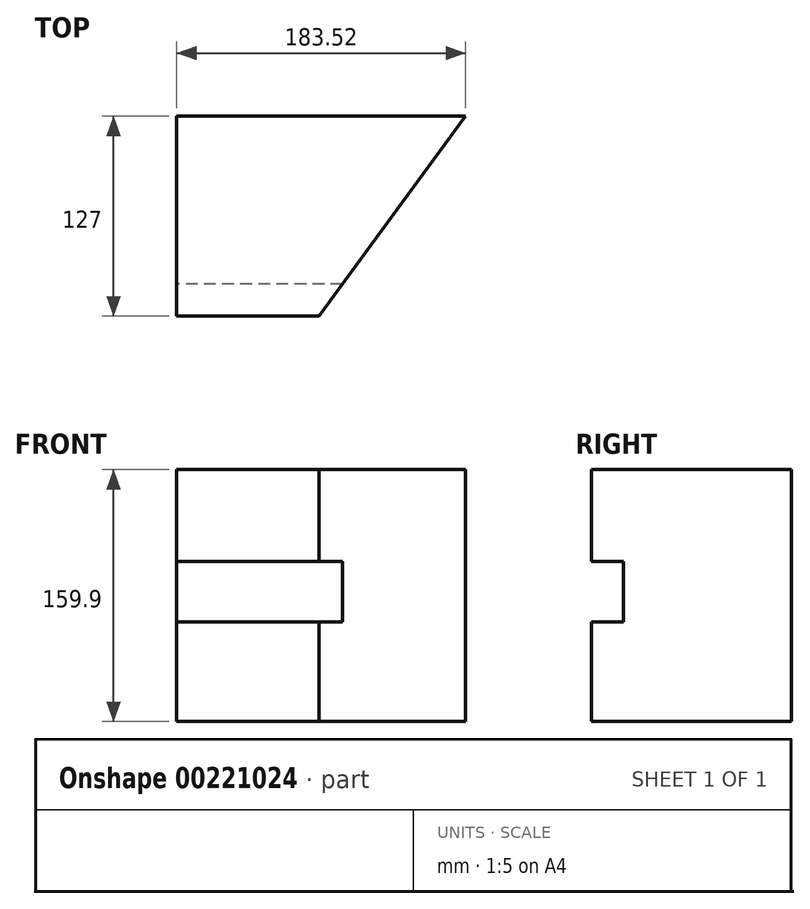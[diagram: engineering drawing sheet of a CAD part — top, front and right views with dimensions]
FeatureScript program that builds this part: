
annotation { "Feature Type Name" : "Feature", "Feature Type Description" : "" }
export const myFeature = defineFeature(function(context is Context, id is Id, definition is map)
    precondition{}
    {
        {
            var Q0;
            Q0=qCreatedBy(makeId("Front.planeOp"),FACE);
            var sketch = newSketch(context, id + "F0", { "sketchPlane" : qUnion([Q0])});
            skLineSegment(sketch, "E0.bottom", {"start": v(-57.95, 53.12) * mm, "end": v(125.57, 53.12) * mm});
            skLineSegment(sketch, "E0.top", {"start": v(-57.95, -106.78) * mm, "end": v(125.57, -106.78) * mm});
            skLineSegment(sketch, "E0.left", {"start": v(-57.95, 53.12) * mm, "end": v(-57.95, -106.78) * mm});
            skLineSegment(sketch, "E0.right", {"start": v(125.57, 53.12) * mm, "end": v(125.57, -106.78) * mm});
            skSolve(sketch);
        }
        {
            var Q0;
            Q0 = qSketchRegion(id + "F0", true);
            extrude(context, id + "F1", {"entities" : qUnion([Q0]), "depth" : 127 * mm});
        }
        {
            var Q0;
            Q0=makeQuery(id+"F1.opExtrude","SWEPT_FACE",FACE,{"disambiguationData":[OSD([sQuery(id+"F0.wireOp",EDGE,"E0.top")])]});
            var sketch = newSketch(context, id + "F2", { "sketchPlane" : qUnion([Q0])});
            skLineSegment(sketch, "E1", {"start": v(125.57, 0) * mm, "end": v(249.78, 14.93) * mm});
            skLineSegment(sketch, "E2", {"start": v(249.78, 14.93) * mm, "end": v(305.62, 25.56) * mm});
            skLineSegment(sketch, "E3", {"start": v(305.62, 25.56) * mm, "end": v(61.16, 201.03) * mm});
            skLineSegment(sketch, "E4", {"start": v(61.16, 201.03) * mm, "end": v(125.57, 0) * mm});
            skSolve(sketch);
        }
        {
            var Q0;
            Q0 = qSketchRegion(id + "F2", true);
            extrude(context, id + "F3", {"entities" : qUnion([Q0]), "operationType" : NewBodyOperationType.REMOVE, "endBound" : BoundingType.THROUGH_ALL, "oppositeDirection" : true, "depth" : 25.4 * mm});
        }
        {
            var Q0;
            Q0=makeQuery(id+"F1.opExtrude","SWEPT_FACE",FACE,{"disambiguationData":[OSD([sQuery(id+"F0.wireOp",EDGE,"E0.bottom")])]});
            var sketch = newSketch(context, id + "F4", { "sketchPlane" : qUnion([Q0])});
            skLineSegment(sketch, "E5", {"start": v(76.98, 0) * mm, "end": v(149.57, 0) * mm});
            skLineSegment(sketch, "E6", {"start": v(149.57, 0) * mm, "end": v(127.33, 0) * mm});
            skLineSegment(sketch, "E7", {"start": v(127.33, 0) * mm, "end": v(125.57, 0) * mm});
            skLineSegment(sketch, "E8", {"start": v(125.57, 0) * mm, "end": v(32.5, -127) * mm});
            skLineSegment(sketch, "E9", {"start": v(32.5, -127) * mm, "end": v(137.35, -127) * mm});
            skLineSegment(sketch, "E10", {"start": v(137.35, -127) * mm, "end": v(149.57, 0) * mm});
            skSolve(sketch);
        }
        {
            var Q0;
            Q0 = qSketchRegion(id + "F4", true);
            extrude(context, id + "F5", {"entities" : qUnion([Q0]), "operationType" : NewBodyOperationType.REMOVE, "endBound" : BoundingType.THROUGH_ALL, "oppositeDirection" : true, "depth" : 25.4 * mm});
        }
        {
            var Q0;
            Q0=makeQuery(id+"F1.opExtrude","SWEPT_FACE",FACE,{"disambiguationData":[OSD([sQuery(id+"F0.wireOp",EDGE,"E0.left")])]});
            var sketch = newSketch(context, id + "F6", { "sketchPlane" : qUnion([Q0])});
            skLineSegment(sketch, "E11", {"start": v(127, -43.63) * mm, "end": v(106.67, -43.63) * mm});
            skLineSegment(sketch, "E12", {"start": v(106.67, -43.63) * mm, "end": v(106.67, -5.27) * mm});
            skLineSegment(sketch, "E13", {"start": v(106.67, -5.27) * mm, "end": v(127, -5.27) * mm});
            skLineSegment(sketch, "E14", {"start": v(127, -5.27) * mm, "end": v(127, -43.63) * mm});
            skSolve(sketch);
        }
        {
            var Q0;
            Q0 = qSketchRegion(id + "F6", true);
            extrude(context, id + "F7", {"entities" : qUnion([Q0]), "operationType" : NewBodyOperationType.REMOVE, "endBound" : BoundingType.THROUGH_ALL, "oppositeDirection" : true, "depth" : 25.4 * mm});
        }
    });
